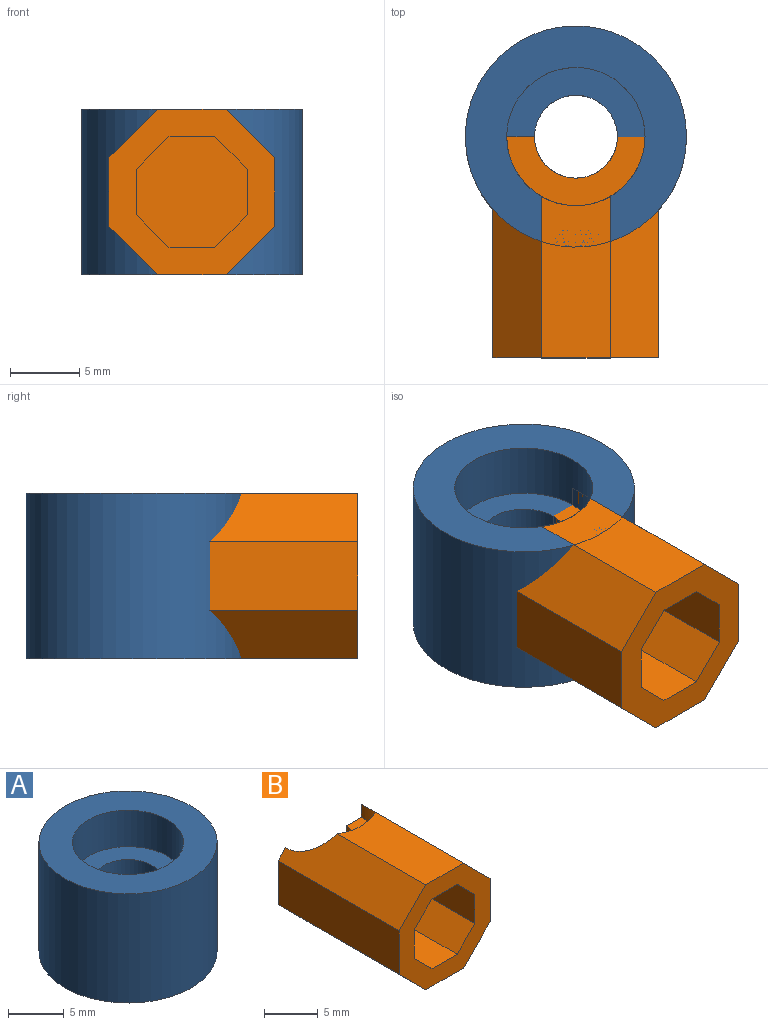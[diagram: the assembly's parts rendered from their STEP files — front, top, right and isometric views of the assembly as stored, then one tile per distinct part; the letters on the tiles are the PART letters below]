
ASSEMBLY  parts=2 mates=1
PART A: 6 faces, bbox 16x16x12 mm
  f0: cylinder r=3mm len=8mm, axis (0,0,1), area 150.8mm2, adj f3,f5
  f1: cylinder r=8mm len=16mm, axis (0,0,-1), area 603.2mm2, adj f2,f3
  f2: plane 16x16mm, normal (0,0,1), area 122.5mm2, adj f1,f4
  f3: plane 16x16mm, normal (0,0,-1), area 172.8mm2, adj f0,f1
  f4: cylinder r=5mm len=10mm, axis (0,0,-1), area 125.7mm2, adj f2,f5
  f5: plane 10x10mm, normal (0,0,1), area 50.3mm2, adj f0,f4
PART B: 23 faces, bbox 12x16x12 mm
  f0: plane 8.97x3mm, normal (0,1,0), area 18.9mm2, adj f3,f8,f17,f20,f21,f22
  f1: plane 8.97x3mm, normal (0,1,0), area 18.9mm2, adj f4,f5,f6,f20,f21,f22
  f2: plane 11.66x4.97mm, normal (0,0,1), area 55.7mm2, adj f3,f4,f18,f21
  f3: plane 16x3.51mm, normal (0.71,0,0.71), area 68.6mm2, adj f0,f2,f17,f18,f21
  f4: plane 16x3.51mm, normal (-0.71,0,0.71), area 68.6mm2, adj f1,f2,f5,f18,f21
  f5: plane 16x4.97mm, normal (-1,0,0), area 79.5mm2, adj f1,f4,f6,f18
  f6: plane 16x3.51mm, normal (-0.71,0,-0.71), area 78.7mm2, adj f1,f5,f7,f18,f20
  f7: plane 14.32x4.97mm, normal (0,0,-1), area 66.6mm2, adj f6,f8,f18,f20
  f8: plane 16x3.51mm, normal (0.71,0,-0.71), area 78.7mm2, adj f0,f7,f17,f18,f20
  f9: plane 6x3.31mm, normal (0,0,-1), area 19.9mm2, adj f10,f16,f18,f19
  f10: plane 6x2.34mm, normal (-0.71,0,-0.71), area 19.9mm2, adj f9,f11,f18,f19
  f11: plane 6x3.31mm, normal (-1,0,0), area 19.9mm2, adj f10,f12,f18,f19
  f12: plane 6x2.34mm, normal (-0.71,0,0.71), area 19.9mm2, adj f11,f13,f18,f19
  f13: plane 6x3.31mm, normal (0,0,1), area 19.9mm2, adj f12,f14,f18,f19
  f14: plane 6x2.34mm, normal (0.71,0,0.71), area 19.9mm2, adj f13,f15,f18,f19
  f15: plane 6x3.31mm, normal (1,0,0), area 19.9mm2, adj f14,f16,f18,f19
  f16: plane 6x2.34mm, normal (0.71,0,-0.71), area 19.9mm2, adj f9,f15,f18,f19
  f17: plane 16x4.97mm, normal (1,0,0), area 79.5mm2, adj f0,f3,f8,f18
  f18: plane 12x12mm, normal (0,-1,0), area 66.3mm2, adj f2,f3,f4,f5,f6,f7,f8,f9
  f19: plane 8x8mm, normal (0,-1,0), area 53mm2, adj f9,f10,f11,f12,f13,f14,f15,f16
  f20: cylinder r=3mm len=8mm, axis (0,0,1), area 74.2mm2, adj f0,f1,f6,f7,f8,f22
  f21: cylinder r=5mm len=10mm, axis (0,0,-1), area 45.6mm2, adj f0,f1,f2,f3,f4,f22
  f22: plane 10x5mm, normal (0,0,1), area 25.1mm2, adj f0,f1,f20,f21
PLACE A rot(axis=(1,0,0),0deg) t=(0,0,0)mm
PLACE B at identity
MATE fastened A.f1 <-> B.f21  axis (0,0,-1) through (0,0,-6)mm
